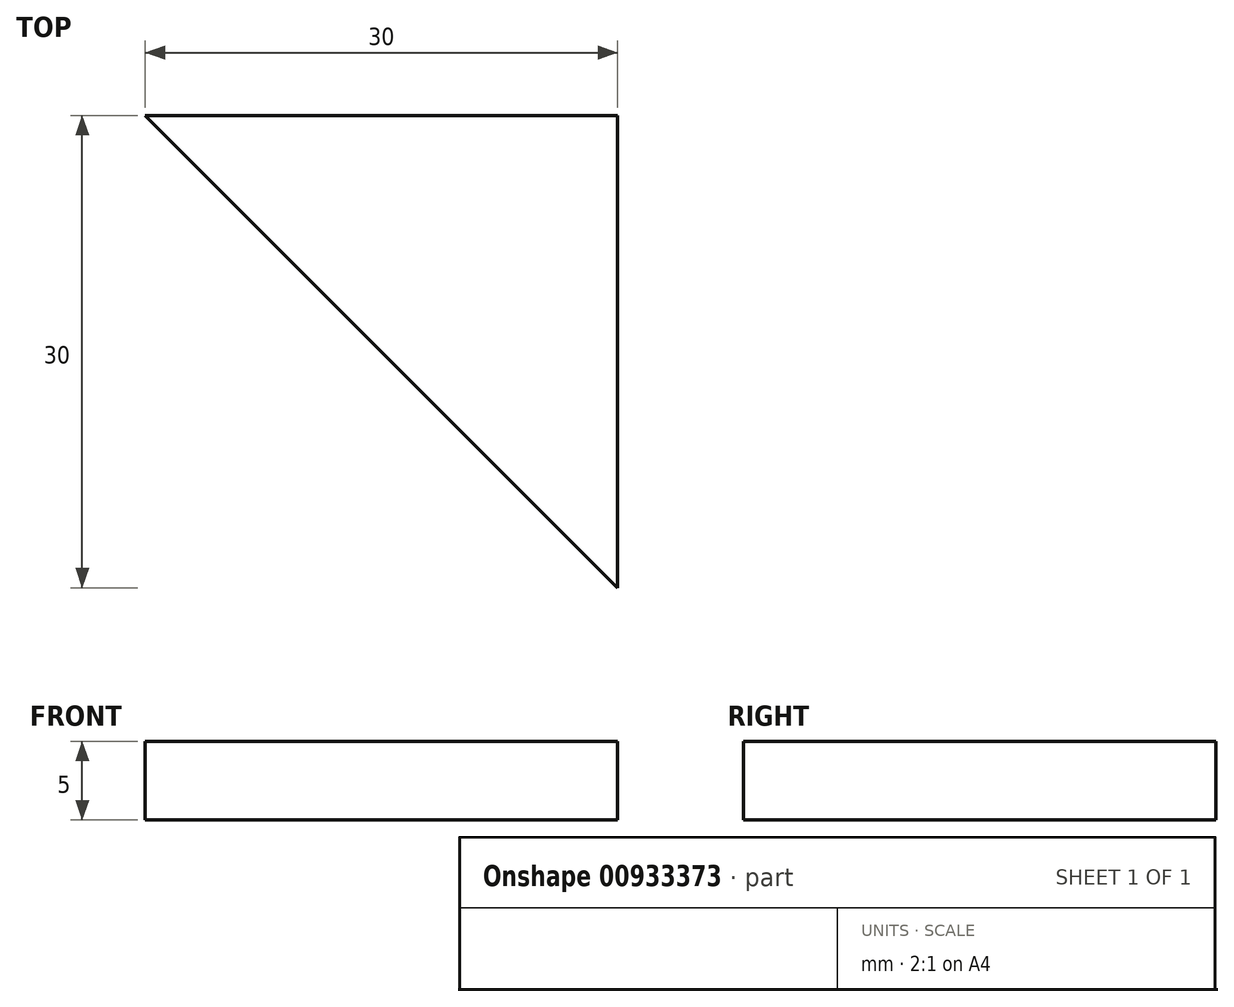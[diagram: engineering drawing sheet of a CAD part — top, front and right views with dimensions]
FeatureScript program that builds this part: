
annotation { "Feature Type Name" : "Feature", "Feature Type Description" : "" }
export const myFeature = defineFeature(function(context is Context, id is Id, definition is map)
    precondition{}
    {
        {
            var Q0;
            Q0=qCreatedBy(makeId("Top.planeOp"),FACE);
            var sketch = newSketch(context, id + "F0", { "sketchPlane" : qUnion([Q0])});
            skLineSegment(sketch, "E0.0", {"start": v(8.66, 15) * mm, "end": v(8.66, -15) * mm});
            skLineSegment(sketch, "E0.1", {"start": v(8.66, -15) * mm, "end": v(-21.34, 15) * mm});
            skLineSegment(sketch, "E0.2", {"start": v(-21.34, 15) * mm, "end": v(8.66, 15) * mm});
            skPoint(sketch, "E0.0.midPoint", {"position": v(8.66, 0) * mm});
            skSolve(sketch);
        }
        {
            var Q0;
            Q0 = qSketchRegion(id + "F0", true);
            extrude(context, id + "F1", {"entities" : qUnion([Q0]), "depth" : 5 * mm, "offsetDistance" : 25 * mm});
        }
    });
